# Revit family: Hager-Typ.B_TP&N_Invicta_3_125A-UK-en
name_source: partatom
category: Electrical Equipment
units: mm (PartAtom-declared; Revit-internal decimal feet)

## family parameters
Cut with Voids When Loaded = No
Host = Face
Panel Configuration = Two Columns, Circuits Across
Part Type = Panelboard
Room Calculation Point = No
Round Connector Dimension = Use Diameter
Shared = No

## types (21) — shared parameters
Classification.Uniclass.Pr.Description = Control circuit device enclosures
Classification.Uniclass.Pr.Number = Pr_80_77_28_16
EF000003 - Mounting method = EV000384 - Surface mounted (plaster)
EF000007 - Colour = EV000154 - Other
EF000008 - Width = 465 mm  [stored 1.52559 ft]
EF000118 - With mounting plate = No
EF001062 - EMC-version = No
EF001134 - DIN-rail = No
EF001596 - Material housing = EV000179 - Steel
EF004462 - Type of closure = EV000154 - Other
EF006306 - With lock = Yes
EF015776 - Earthing terminal block = Yes
EF015777 - Neutral terminal block = Yes
EF015941 - Signal passing door = No
HG000002 - With door or cover = Yes
HG000003 - Range = Type B TP&N Distribution Boards
HG000005 - Thickness = 3 mm  [stored 0.00984252 ft]
HG000017 - Distance between poles = 18 mm  [stored 0.0590551 ft]
Manufacturer = Hager
Type Comments = Type B TP&N Distribution Boards
zero-valued in all types: Default Elevation, EF000218 - Built-in depth, EF000266 - Number of rows, EF000332 - Built-in height, EF000846 - Built-in width, EF001131 - Internal depth

## per-type parameters (varying)
| type | EF000040 - Height | EF000049 - Depth | EF000116 - RAL-number | EF000339 - Type of cover | EF001088 - Extension possible | EF002950 - Width in number of modular spacings | EF005474 - Degree of protection (IP) | EF006244 - Transparent cover/door | HG000004 - Manufacturer reference | Model |
| Surface mounted IP30 W465 H1100 D132.5 27 Modular spacings - JK118B | 1100 mm | 132 mm  [stored 0.433071 ft] | 7035 | EV001012 - Cover | No | 27 | EV006410 - IP30 | No | JK118B | JK118B |
| Surface mounted IP30 W465 H1100 D132.5 27 Modular spacings - JK118BG | 1100 mm | 132 mm  [stored 0.433071 ft] | 7035 | EV001012 - Cover | No | 27 | EV006410 - IP30 | Yes | JK118BG | JK118BG |
| Surface mounted IP30 W465 H1100 D165.5 27 Modular spacings - JK118BA3 | 1100 mm | 166 mm | 7035 | EV004216 - Door | No | 27 | EV006410 - IP30 | No | JK118BA3 | JK118BA3 |
| Surface mounted IP30 W465 H1250 D132.5 36 Modular spacings - JK124B | 1250 mm  [stored 4.10105 ft] | 132 mm  [stored 0.433071 ft] |  | EV001012 - Cover | No | 36 | EV006410 - IP30 | No | JK124B | JK124B |
| Surface mounted IP30 W465 H1250 D132.5 36 Modular spacings - JK124BG | 1250 mm  [stored 4.10105 ft] | 132 mm  [stored 0.433071 ft] | 7035 | EV001012 - Cover | No | 36 | EV006410 - IP30 | Yes | JK124BG | JK124BG |
| Surface mounted IP30 W465 H1250 D165.5 36 Modular spacings - JK124BA3 | 1250 mm  [stored 4.10105 ft] | 166 mm | 7035 | EV004216 - Door | No | 36 | EV006410 - IP30 | No | JK124BA3 | JK124BA3 |
| Surface mounted IP30 W465 H500 D132.5 6 Modular spacings - JK104B | 500 mm  [stored 1.64042 ft] | 132 mm  [stored 0.433071 ft] | 7035 | EV001012 - Cover | No | 6 | EV006410 - IP30 | No | JK104B | JK104B |
| Surface mounted IP30 W465 H500 D132.5 6 Modular spacings - JK104BA3 | 500 mm  [stored 1.64042 ft] | 132 mm  [stored 0.433071 ft] | 7035 | EV004216 - Door | No | 6 | EV006410 - IP30 | No | JK104BA3 | JK104BA3 |
| Surface mounted IP30 W465 H500 D132.5 6 Modular spacings - JK104BG | 500 mm  [stored 1.64042 ft] | 132 mm  [stored 0.433071 ft] | 7035 | EV001012 - Cover | No | 6 | EV006410 - IP30 | Yes | JK104BG | JK104BG |
| Surface mounted IP30 W465 H550 D132.5 9 Modular spacings - JK106B | 550 mm | 132 mm  [stored 0.433071 ft] | 7035 | EV001012 - Cover | No | 9 | EV006410 - IP30 | No | JK106B | JK106B |
| Surface mounted IP30 W465 H550 D132.5 9 Modular spacings - JK106BA3 | 550 mm | 132 mm  [stored 0.433071 ft] | 7035 | EV004216 - Door | No | 9 | EV006410 - IP30 | No | JK106BA3 | JK106BA3 |
| Surface mounted IP30 W465 H550 D132.5 9 Modular spacings - JK106BG | 550 mm | 132 mm  [stored 0.433071 ft] | 7035 | EV001012 - Cover | No | 9 | EV006410 - IP30 | Yes | JK106BG | JK106BG |
| Surface mounted IP30 W465 H625 D132.5 12 Modular spacings - JK108B | 625 mm | 132 mm  [stored 0.433071 ft] | 7035 | EV001012 - Cover | No | 12 | EV006410 - IP30 | No | JK108B | JK108B |
| Surface mounted IP30 W465 H625 D132.5 12 Modular spacings - JK108BA3 | 625 mm | 132 mm  [stored 0.433071 ft] | 7035 | EV004216 - Door | No | 12 | EV006410 - IP30 | No | JK108BA3 | JK108BA3 |
| Surface mounted IP30 W465 H625 D132.5 12 Modular spacings - JK108BG | 625 mm | 132 mm  [stored 0.433071 ft] | 7035 | EV001012 - Cover | No | 12 | EV006410 - IP30 | Yes | JK108BG | JK108BG |
| Surface mounted IP30 W465 H850 D132.5 18 Modular spacings - JK112B | 850 mm  [stored 2.78871 ft] | 132 mm  [stored 0.433071 ft] | 7035 | EV001012 - Cover | No | 18 | EV006410 - IP30 | No | JK112B | JK112B |
| Surface mounted IP30 W465 H850 D165.5 18 Modular spacings - JK112BA3 | 850 mm  [stored 2.78871 ft] | 166 mm | 7035 | EV004216 - Door | No | 18 | EV006410 - IP30 | No | JK112BA3 | JK112BA3 |
| Surface mounted IP30 W465 H950 D132.5 24 Modular spacings - JK116B | 950 mm | 132 mm  [stored 0.433071 ft] | 7035 | EV001012 - Cover | No | 24 | EV006410 - IP30 | No | JK116B | JK116B |
| Surface mounted IP30 W465 H950 D132.5 24 Modular spacings - JK116BG | 950 mm | 132 mm  [stored 0.433071 ft] | 7035 | EV001012 - Cover | Yes | 24 | EV006410 - IP30 | Yes | JK116BG | JK116BG |
| Surface mounted IP30 W465 H950 D165.5 24 Modular spacings - JK116BA3 | 950 mm | 166 mm | 7035 | EV004216 - Door | No | 24 | EV006410 - IP30 | No | JK116BA3 | JK116BA3 |
| Surface mounted IP3X W465 H850 D132.5 18 Modular spacings - JK112BG | 850 mm  [stored 2.78871 ft] | 132 mm  [stored 0.433071 ft] | 7035 | EV001012 - Cover | No | 18 | EV006414 - IP3X | Yes | JK112BG | JK112BG |

note: [stored X ft] marks values corroborated as IEEE doubles in the binary element streams (Revit-internal decimal feet)

## geometry (parser evidence)
native form markers: Sweep x7
no freeform markers — native parametric forms only
